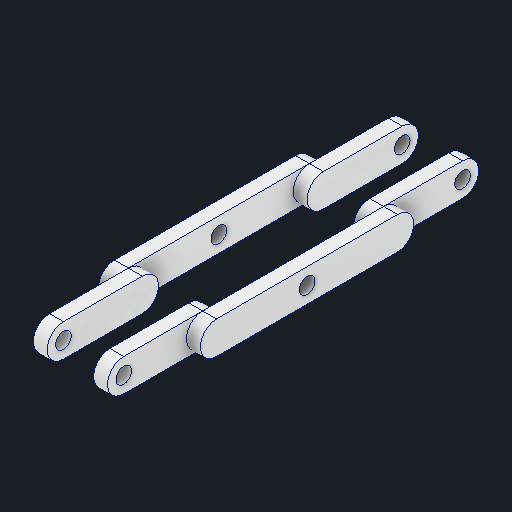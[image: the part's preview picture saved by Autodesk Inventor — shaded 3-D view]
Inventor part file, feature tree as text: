
AUTODESK INVENTOR PART (.ipt)
format: ipt  version: 2025.3 (Build 293356030, 356C)  size: 307,200 bytes
history: native  units: mm
features: extrude x4, sketch x3, hole x2
ambient origin geometry x8: Origin, YZ Plane, XZ Plane, XY Plane, X Axis, Y Axis, Z Axis, Center Point
bodies: Body1 (feature_tree)
feature tree (9):
  sketch  "Sketch1"  dims[d17=5.0mm d18=80.0mm]
  extrude  "Extrusión3"  Depth=80.0mm
  extrude  "Extrusión4"  Depth=7.0mm
  extrude  "Extrusión5"  Depth=16.0mm TaperAngle=0.0deg
  extrude  "Extrusión6"  Depth=8.0mm
  hole  "Agujero1"  [1 undecoded]
  hole  "Agujero2"  [1 undecoded]
  sketch  "Boceto2"  dims[d19=3.0mm d20=7.0mm]
  sketch  "Boceto3"  dims[d21=22.0mm d22=0.0mm d23=16.0mm d24=0.0mm d25=3.4mm d26=6.0mm d27=6.3mm d28=2.0mm d29=90.0deg d30=8.0mm d31=20.594885mm d32=39.0mm d33=16.0mm d34=0.0mm d35=10.0mm d36=0.0mm d37=3.4mm d38=6.0mm d39=6.3mm d40=2.0mm d41=90.0deg d42=8.0mm d43=20.594885mm]
note: 2 required parameter values undecoded (feature->parameter linkage not recoverable at this tier; creation-order binding heuristic only, values carry confidence <= 0.55)
